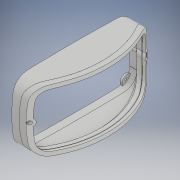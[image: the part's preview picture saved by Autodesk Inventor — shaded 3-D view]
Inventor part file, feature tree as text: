
AUTODESK INVENTOR PART (.ipt)
format: ipt  version: 2019 (Build 230136000, 136)  size: 3,335,168 bytes
history: native  units: mm
features: extrude x15, sketch x11, projected_geometry x7, other x4, hole x3, plane x3, fillet x1
ambient origin geometry x8: Origin, YZ Plane, XZ Plane, XY Plane, X Axis, Y Axis, Z Axis, Center Point
bodies: Volumenkörper3 (feature_tree), Volumenkörper7 (feature_tree), Volumenkörper8 (feature_tree), Volumenkörper9 (feature_tree), Volumenkörper11 (feature_tree)
feature tree (44):
  sketch  "Skizze1"  dims[d8=1.000002mm d10=3.000002mm]
  extrude  "Extrusion3"  Depth=3.000002mm
  extrude  "Extrusion4"  Depth=10.0mm TaperAngle=0.0deg
  sketch  "Skizze2"  dims[d11=1.2mm d12=0.0mm d13=10.0mm d14=0.0mm]
  extrude  "Extrusion5"  Depth=8.0mm
  sketch  "Skizze3"  dims[d16=8.0mm d17=8.0mm]
  hole  "Bohrung1"  [1 undecoded]
  extrude  "Extrusion7"  Depth=138.0mm
  plane  "Arbeitsebene1"
  plane  "Arbeitsebene2"
  extrude  "Extrusion14"  Depth=10.0mm TaperAngle=0.0deg
  sketch  "Skizze7"  dims[d20=3.0mm d21=0.0mm]
  extrude  "Extrusion11"  Depth=140.0mm
  extrude  "Extrusion15"  Depth=3.0mm
  extrude  "Extrusion13"  Depth=6.0mm
  extrude  "Extrusion16"  Depth=3.000001mm
  extrude  "Extrusion17"  Depth=40.0mm TaperAngle=0.0deg
  extrude  "Extrusion20"  Depth=50.0mm TaperAngle=0.0deg
  extrude  "Extrusion21"  Depth=40.0mm TaperAngle=0.0deg
  other  "Kombinieren1"
  extrude  "Extrusion22"  Depth=0.499998mm
  other  "Kombinieren2"
  fillet  "Rundung1"  Radius=50.0mm
  plane  "Arbeitsebene4"
  sketch  "Skizze17"  dims[d49=3.0mm d50=3.0mm]
  hole  "Bohrung3"  [1 undecoded]
  hole  "Bohrung4"  [1 undecoded]
  extrude  "Extrusion25"  Depth=40.0mm TaperAngle=0.0deg
  other  "Kombinieren4"
  extrude  "Extrusion26"  Depth=0.75mm
  other  "Bild1"
  projected_geometry  "Projizierte Kontur1"
  sketch  "Skizze6"  dims[d18=8.0mm d19=8.0mm]
  projected_geometry  "Projizierte Kontur3"
  sketch  "Skizze9"  dims[d26=3.5mm d27=6.0mm d28=4.0mm d29=2.0mm d30=90.0deg d31=8.0mm d32=20.594885mm d33=138.0mm]
  projected_geometry  "Projizierte Kontur4"
  sketch  "Skizze10"  dims[d34=138.0mm d35=10.0mm d36=0.0mm]
  projected_geometry  "Projizierte Kontur5"
  sketch  "Skizze12"  dims[d43=40.0mm d44=0.0mm d45=140.0mm]
  projected_geometry  "Projizierte Kontur7"
  projected_geometry  "Projizierte Kontur10"
  sketch  "Skizze18"  dims[d51=40.0mm d52=0.0mm d53=6.0mm]
  sketch  "Skizze19"  dims[d54=40.0mm d55=0.0mm d56=3.000001mm d57=40.0mm d58=0.0mm d59=50.0mm d60=0.0mm d61=40.0mm d62=0.0mm d63=0.499998mm d69=50.0mm d70=0.0mm d71=40.0mm d72=0.0mm d73=5.0mm d74=40.0mm d75=0.0mm d76=0.75mm d77=3.0mm d95=50.0mm d96=6.0mm d97=6.0mm d98=3.0mm d99=6.0mm d100=4.0mm d101=2.0mm d102=90.0deg d103=8.0mm d104=20.594885mm d105=5.5mm d106=6.0mm d107=4.0mm d108=2.0mm d109=90.0deg d110=30.0mm d111=0.0mm d112=40.0mm d113=0.0mm d114=10.0mm d115=0.0mm]
  projected_geometry  "Projizierte Kontur11"
note: 3 required parameter values undecoded (feature->parameter linkage not recoverable at this tier; creation-order binding heuristic only, values carry confidence <= 0.55)
